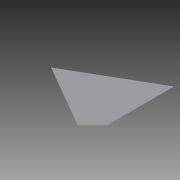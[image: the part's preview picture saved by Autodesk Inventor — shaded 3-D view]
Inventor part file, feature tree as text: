
AUTODESK INVENTOR PART (.ipt)
format: ipt  version: 2016 (Build 200138000, 138)  size: 66,048 bytes
history: native  units: in
note: dims shown in document units (in); Inventor stores cm internally (conversion verified against a paired STEP export)
features: extrude x1, sketch x1
ambient origin geometry x8: Origin, YZ Plane, XZ Plane, XY Plane, X Axis, Y Axis, Z Axis, Center Point
bodies: Solid1 (feature_tree)
feature tree (2):
  extrude  "Extrusion1"  Depth=0.02in TaperAngle=0.0deg
  sketch  "Sketch1"  dims[d2=84.0in d3=0.02in d4=0.0in]
